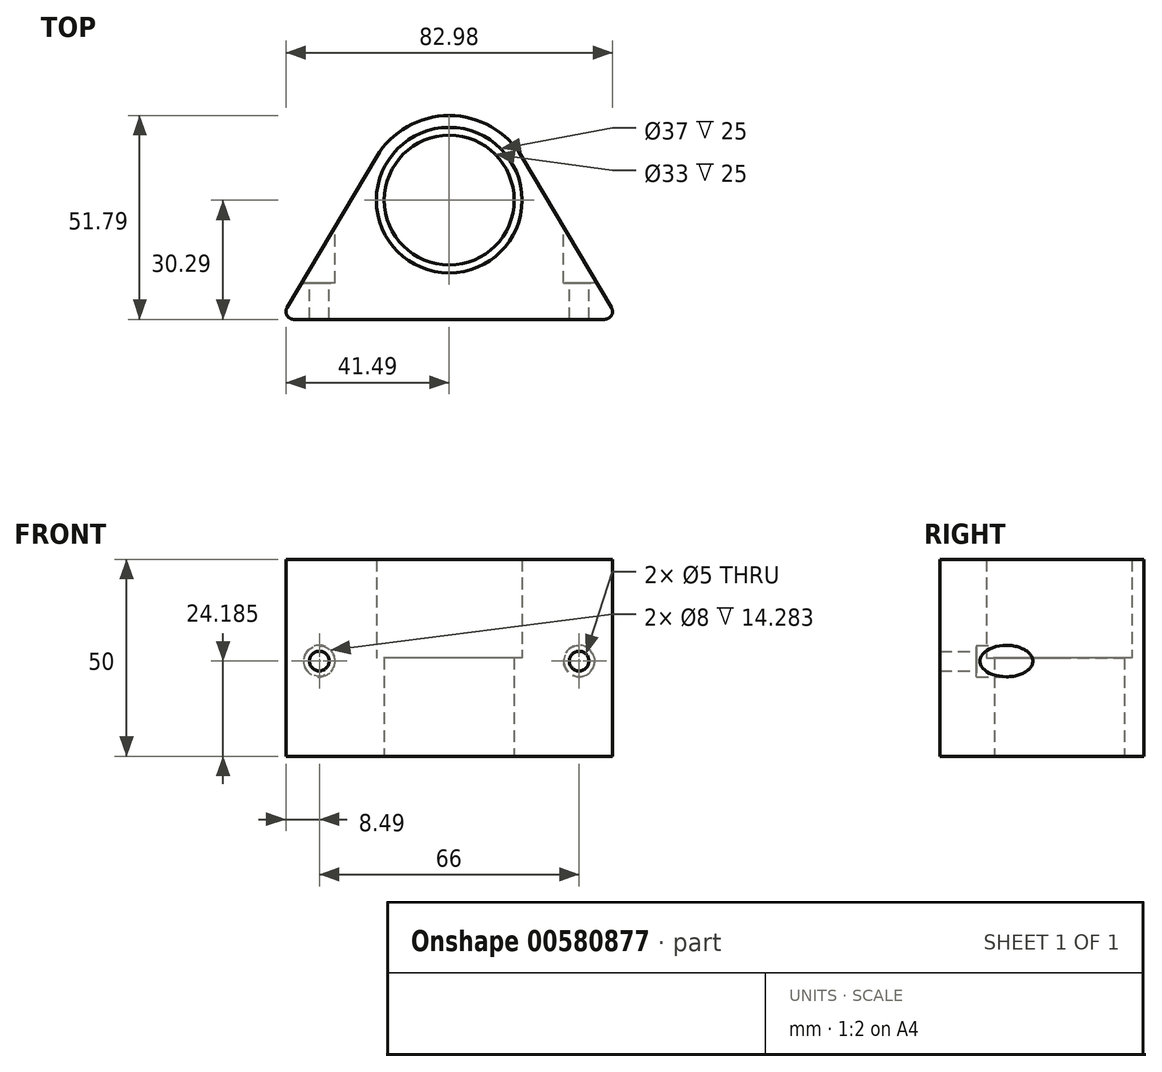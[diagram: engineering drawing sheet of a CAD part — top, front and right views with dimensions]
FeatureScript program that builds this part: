
annotation { "Feature Type Name" : "Feature", "Feature Type Description" : "" }
export const myFeature = defineFeature(function(context is Context, id is Id, definition is map)
    precondition{}
    {
        {
            var Q0;
            Q0=qCreatedBy(makeId("Top.planeOp"),FACE);
            var sketch = newSketch(context, id + "F0", { "sketchPlane" : qUnion([Q0])});
            skCircle(sketch, "E0", {"center": v(0, 0) * mm, "radius": 18.5 * mm});
            skCircle(sketch, "E1", {"center": v(0, 0) * mm, "radius": 16.5 * mm});
            skCircle(sketch, "E2", {"center": v(0, 0) * mm, "radius": 21.5 * mm});
            skLineSegment(sketch, "E3", {"start": v(0, -30.29) * mm, "end": v(39.49, -30.29) * mm});
            skLineSegment(sketch, "E4", {"start": v(41.2, -27.26) * mm, "end": v(18.48, 10.98) * mm});
            skLineSegment(sketch, "E5", {"start": v(0, -30.29) * mm, "end": v(-39.49, -30.29) * mm});
            skLineSegment(sketch, "E6", {"start": v(-41.2, -27.26) * mm, "end": v(-18.48, 10.98) * mm});
            skPoint(sketch, "E7.visualSharp", {"position": v(-43, -30.29) * mm});
            skArc(sketch, "E7.filletArc", {"start": v(-41.2, -27.26) * mm, "mid": v(-41.22, -29.28) * mm, "end": v(-39.49, -30.29) * mm});
            skPoint(sketch, "E8.visualSharp", {"position": v(43, -30.29) * mm});
            skArc(sketch, "E8.filletArc", {"start": v(39.49, -30.29) * mm, "mid": v(41.22, -29.28) * mm, "end": v(41.2, -27.26) * mm});
            skSolve(sketch);
        }
        {
            var Q0;
            Q0=makeQuery(id+"F0.imprint","IMPRINT",FACE,{"disambiguationData":[TD([[makeQuery(id+"F0.imprint","IMPRINT",EDGE,{"derivedFrom":sQuery(id+"F0.wireOp",EDGE,"E3")}),1.0]])]});
            var Q1;
            Q1=makeQuery(id+"F0.imprint","IMPRINT",FACE,{"disambiguationData":[TD([[makeQuery(id+"F0.imprint","IMPRINT",EDGE,{"derivedFrom":sQuery(id+"F0.wireOp",EDGE,"E0")}),-1.0]])]});
            extrude(context, id + "F1", {"entities" : qUnion([Q0, Q1]), "depth" : 50 * mm, "offsetDistance" : 25 * mm});
        }
        {
            var Q0;
            Q0=makeQuery(id+"F0.imprint","IMPRINT",FACE,{"disambiguationData":[TD([[makeQuery(id+"F0.imprint","IMPRINT",EDGE,{"derivedFrom":sQuery(id+"F0.wireOp",EDGE,"E0")}),1.0]])]});
            extrude(context, id + "F2", {"entities" : qUnion([Q0]), "operationType" : NewBodyOperationType.ADD, "depth" : 25 * mm, "offsetDistance" : 25 * mm});
        }
        {
            var Q0;
            Q0=qCreatedBy(makeId("Front.planeOp"),FACE);
            var sketch = newSketch(context, id + "F3", { "sketchPlane" : qUnion([Q0])});
            skLineSegment(sketch, "E9.bottom", {"start": v(43, 49.18) * mm, "end": v(-43, 49.18) * mm});
            skLineSegment(sketch, "E9.top", {"start": v(43, -0.82) * mm, "end": v(-43, -0.82) * mm});
            skLineSegment(sketch, "E9.left", {"start": v(43, 49.18) * mm, "end": v(43, -0.82) * mm});
            skLineSegment(sketch, "E9.right", {"start": v(-43, 49.18) * mm, "end": v(-43, -0.82) * mm});
            skPoint(sketch, "E9.middle", {"position": v(0, 24.18) * mm});
            skCircle(sketch, "E10", {"center": v(33, 24.18) * mm, "radius": 2.5 * mm});
            skCircle(sketch, "E11", {"center": v(-33, 24.18) * mm, "radius": 2.5 * mm});
            skCircle(sketch, "E12", {"center": v(-33, 24.18) * mm, "radius": 4 * mm});
            skCircle(sketch, "E13", {"center": v(33, 24.18) * mm, "radius": 4 * mm});
            skSolve(sketch);
        }
        {
            var Q0;
            Q0=makeQuery(id+"F3.imprint","IMPRINT",FACE,{"disambiguationData":[TD([[makeQuery(id+"F3.imprint","IMPRINT",EDGE,{"derivedFrom":sQuery(id+"F3.wireOp",EDGE,"E10")}),1.0]])]});
            var Q1;
            Q1=makeQuery(id+"F3.imprint","IMPRINT",FACE,{"disambiguationData":[TD([[makeQuery(id+"F3.imprint","IMPRINT",EDGE,{"derivedFrom":sQuery(id+"F3.wireOp",EDGE,"E11")}),1.0]])]});
            extrude(context, id + "F4", {"entities" : qUnion([Q0, Q1]), "operationType" : NewBodyOperationType.REMOVE, "depth" : 35 * mm, "offsetDistance" : 25 * mm});
        }
        {
            var Q0;
            Q0=makeQuery(id+"F3.imprint","IMPRINT",FACE,{"disambiguationData":[TD([[makeQuery(id+"F3.imprint","IMPRINT",EDGE,{"derivedFrom":sQuery(id+"F3.wireOp",EDGE,"E10")}),-1.0]])]});
            var Q1;
            Q1=makeQuery(id+"F3.imprint","IMPRINT",FACE,{"disambiguationData":[TD([[makeQuery(id+"F3.imprint","IMPRINT",EDGE,{"derivedFrom":sQuery(id+"F3.wireOp",EDGE,"E11")}),-1.0]])]});
            extrude(context, id + "F5", {"entities" : qUnion([Q0, Q1]), "operationType" : NewBodyOperationType.REMOVE, "depth" : 21 * mm, "offsetDistance" : 25 * mm});
        }
    });
